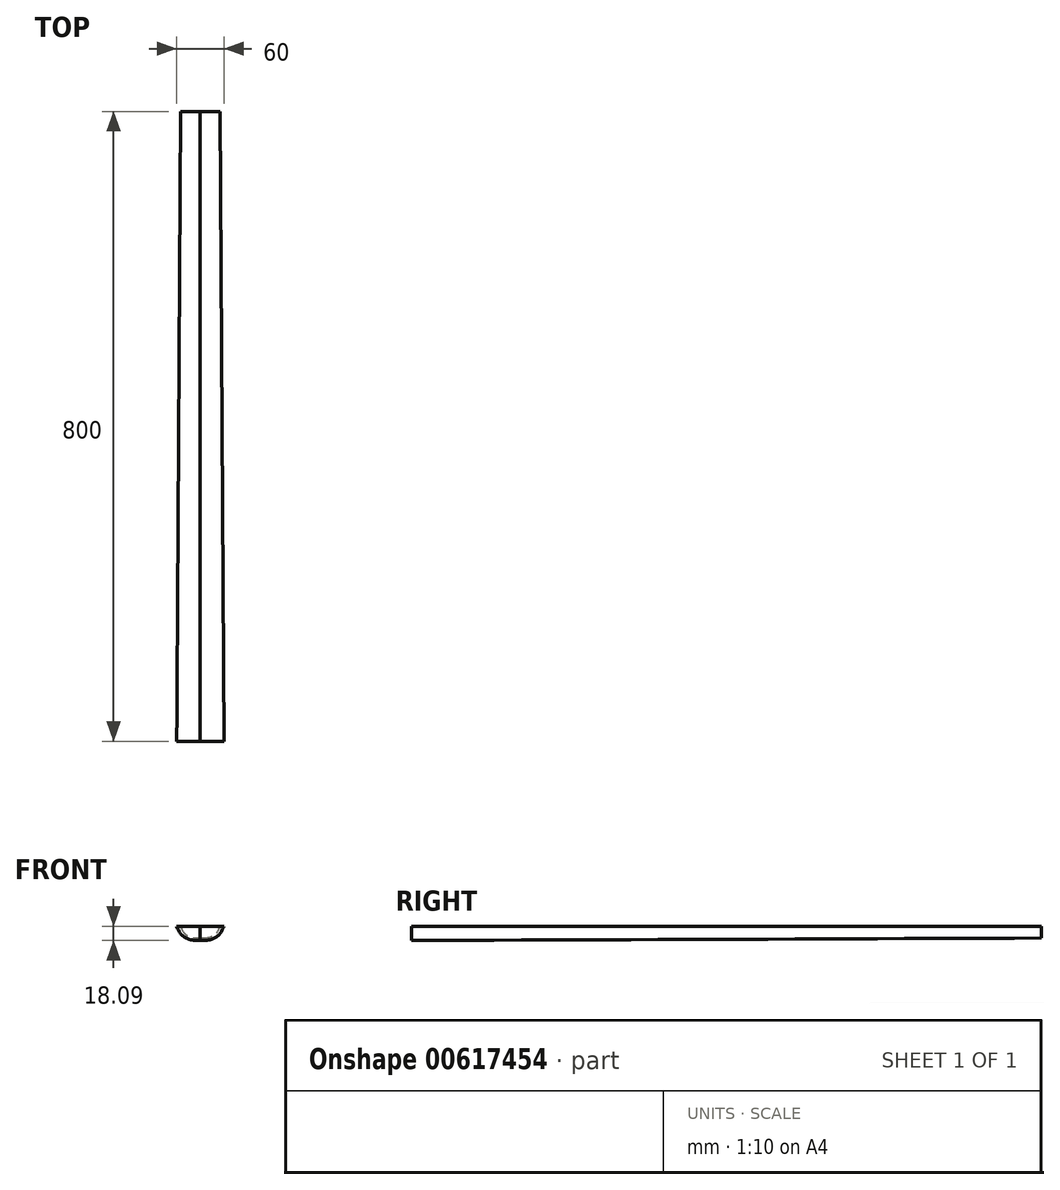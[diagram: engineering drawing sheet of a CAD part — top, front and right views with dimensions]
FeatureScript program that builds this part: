
annotation { "Feature Type Name" : "Feature", "Feature Type Description" : "" }
export const myFeature = defineFeature(function(context is Context, id is Id, definition is map)
    precondition{}
    {
        {
            var Q0;
            Q0=qCreatedBy(makeId("Front.planeOp"),FACE);
            var sketch = newSketch(context, id + "F0", { "sketchPlane" : qUnion([Q0])});
            skLineSegment(sketch, "E0", {"start": v(0, 0) * mm, "end": v(0, -18) * mm});
            skLineSegment(sketch, "E1", {"start": v(0, 0) * mm, "end": v(30, 0) * mm});
            skFitSpline(sketch, "E2", {"points": [v(0, -18) * mm, v(21.36, -12.99) * mm, v(30, 0) * mm], "startDerivative": vector(56.36, -3.15) * mm, "endDerivative": vector(16.66, 42.47) * mm});
            skSolve(sketch);
        }
        {
            var Q0;
            Q0=qCreatedBy(makeId("Front.planeOp"),FACE);
            cPlane(context, id + "F1", {"entities" : qUnion([Q0]), "cplaneType" : CPlaneType.OFFSET, "offset" : 800 * mm, "oppositeDirection" : true, "width" : 150 * mm, "height" : 150 * mm});
        }
        {
            var Q0;
            Q0=qCreatedBy(id+"F1.planeOp",FACE);
            var sketch = newSketch(context, id + "F2", { "sketchPlane" : qUnion([Q0])});
            skLineSegment(sketch, "E3", {"start": v(0, 0) * mm, "end": v(0, -15) * mm});
            skLineSegment(sketch, "E4", {"start": v(0, 0) * mm, "end": v(25, 0) * mm});
            skFitSpline(sketch, "E5", {"points": [v(0, -15) * mm, v(18.67, -10.34) * mm, v(25, 0) * mm], "startDerivative": vector(56.36, -3.15) * mm, "endDerivative": vector(16.66, 42.47) * mm});
            skSolve(sketch);
        }
        {
            var Q0;
            Q0 = qSketchRegion(id + "F0", true);
            var Q1;
            Q1 = qSketchRegion(id + "F2", true);
            loft(context, id + "F3", {"sheetProfilesArray" : [{ "sheetProfileEntities" : qUnion([Q0]) }, { "sheetProfileEntities" : qUnion([Q1]) }]});
        }
        {
            var Q0;
            Q0=makeQuery(id+"F3.opLoft","SWEPT_BODY",BODY,{"disambiguationData":[OSD([makeQuery(id+"F0.imprint","IMPRINT",FACE,{"disambiguationData":[TD([[makeQuery(id+"F0.imprint","IMPRINT",EDGE,{"derivedFrom":sQuery(id+"F0.wireOp",EDGE,"E0")}),1.0]])]}),makeQuery(id+"F2.imprint","IMPRINT",FACE,{"disambiguationData":[TD([[makeQuery(id+"F2.imprint","IMPRINT",EDGE,{"derivedFrom":sQuery(id+"F2.wireOp",EDGE,"E3")}),1.0]])]})])]});
            var Q1;
            {var subQ0=sQuery(id+"F2.wireOp",EDGE,"E3");var subQ1=sQuery(id+"F2.wireOp",EDGE,"E5");var subQ2=sQuery(id+"F2.wireOp",EDGE,"E4");var subQ3=sQuery(id+"F0.wireOp",EDGE,"E0");var subQ4=sQuery(id+"F0.wireOp",EDGE,"E2");var subQ5=sQuery(id+"F0.wireOp",EDGE,"E1");Q1=makeQuery(id+"F3.opLoft","SWEPT_FACE",FACE,{"disambiguationData":[OSD([subQ3,subQ5,subQ4,subQ0,subQ2,subQ1]),TDD([makeQuery(id+"F0.imprint","INTERSECT",VERTEX,{"derivedFrom":[subQ3,subQ5]}),makeQuery(id+"F0.imprint","INTERSECT",VERTEX,{"derivedFrom":[subQ3,subQ4]}),makeQuery(id+"F0.imprint","IMPRINT",EDGE,{"derivedFrom":subQ3}),makeQuery(id+"F2.imprint","INTERSECT",VERTEX,{"derivedFrom":[subQ0,subQ2]}),makeQuery(id+"F2.imprint","INTERSECT",VERTEX,{"derivedFrom":[subQ0,subQ1]}),makeQuery(id+"F2.imprint","IMPRINT",EDGE,{"derivedFrom":subQ0})])]});}
            mirror(context, id + "F4", {"entities" : qUnion([Q0]), "mirrorPlane" : qUnion([Q1])});
        }
    });
